# Revit family: Legrand - Distribution enclosure - XL³ S 4000 -  Métal - 16 modules - h=2200
name_source: partatom
category: Equipement électrique
units: mm (PartAtom-declared; Revit-internal decimal feet)

## family parameters
Basée sur le plan de construction = Non
Configuration du panneau = Deux colonnes, circuits au sein
Cote de connecteur circulaire = Utiliser le diamètre
Couper avec des vides une fois chargée = Non
Numéro OmniClass = 23.80.30.11.17
Partagée = Non
Point de calcul de pièce = Non
Titre OmniClass = Distribution Boards and Control Panels
Toujours verticalement = Oui
Type d'élément = Tableau de raccordement

## types (3) — shared parameters
ETIM Class 6.0 = EC000261
Fabricant = Legrand
General Conditions of Use = https://export.legrand.com
IK = 07
IP = 40
Material = Steel
RAL = 9003
URL = www.legrand.fr
door = Oui
finish kit = Non
finish kit depth 400mm = Non
finish kit depth 600mm = Non
finish kit depth 800mm = Non
left side panel = Oui
plinth 100mm = Non
plinth 200mm = Non
plinth depth 400mm = Non
plinth depth 400mm height 200mm = Non
plinth depth 600mm = Non
plinth depth 600mm height 200mm = Non
plinth depth 800mm = Non
plinth depth 800mm height 200mm = Non
rear panel = Oui
right side panel = Oui
zero-valued in all types: Elévation par défaut, height plinth

## per-type parameters (varying)
| type | Description | depth 400mm | depth 600mm | depth 800mm | door depth 400mm | door depth 600mm | door depth 800mm | left side panel depth 400mm | left side panel depth 600mm | left side panel depth 800mm | right side panel depth 400mm | right side panel depth 600mm | right side panel depth 800mm | structure 338021 | structure 338025 | structure 338029 |
| Legrand - Distribution enclosure - XL³ S 4000 -  Métal - 16 modules - h=2200 - depth 400 | Ref 338021 + 338091 + 338071 + 338111 - Legrand - Distribution enclosure - XL³ S 4000 -  Métal - 16 modules - h=2200 - depth 400 | Oui | Non | Non | Oui | Non | Non | Oui | Non | Non | Oui | Non | Non | Oui | Non | Non |
| Legrand - Distribution enclosure - XL³ S 4000 -  Métal - 16 modules - h=2200 - depth 600 | Ref 338025 + 338091 + 338072 + 338111 - Legrand - Distribution enclosure - XL³ S 4000 -  Métal - 16 modules - h=2200 - depth 600 | Non | Oui | Non | Non | Oui | Non | Non | Oui | Non | Non | Oui | Non | Non | Oui | Non |
| Legrand - Distribution enclosure - XL³ S 4000 -  Métal - 16 modules - h=2200 - depth 800 | Ref 338029 + 338091 + 338073 + 338111 - Legrand - Distribution enclosure - XL³ S 4000 -  Métal - 16 modules - h=2200 - depth 800 | Non | Non | Oui | Non | Non | Oui | Non | Non | Oui | Non | Non | Oui | Non | Non | Oui |
